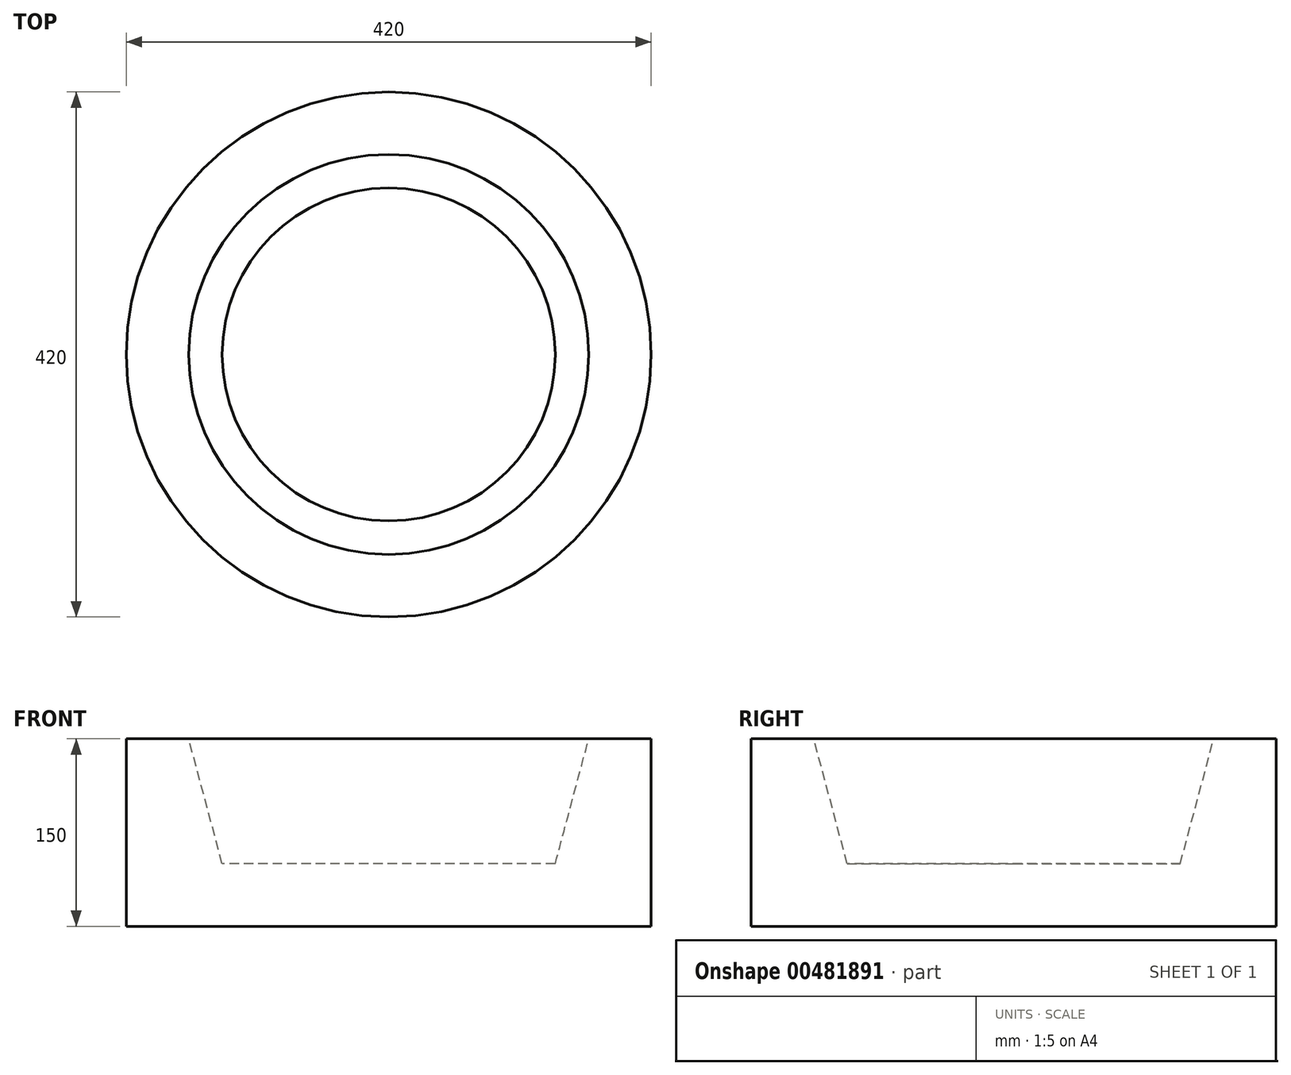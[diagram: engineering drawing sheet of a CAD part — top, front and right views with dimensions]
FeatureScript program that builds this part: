
annotation { "Feature Type Name" : "Feature", "Feature Type Description" : "" }
export const myFeature = defineFeature(function(context is Context, id is Id, definition is map)
    precondition{}
    {
        {
            var Q0;
            Q0=qCreatedBy(makeId("Top.planeOp"),FACE);
            var sketch = newSketch(context, id + "F0", { "sketchPlane" : qUnion([Q0])});
            skCircle(sketch, "E0", {"center": v(0, 0) * mm, "radius": 210 * mm});
            skSolve(sketch);
        }
        {
            var Q0;
            Q0 = qSketchRegion(id + "F0", true);
            extrude(context, id + "F1", {"entities" : qUnion([Q0]), "depth" : 150 * mm});
        }
        {
            var Q0;
            Q0=makeQuery(id+"F1.opExtrude","CAP_FACE",FACE,{"disambiguationData":[OSD([sQuery(id+"F0.wireOp",EDGE,"E0")])],"isStart":false});
            var sketch = newSketch(context, id + "F2", { "sketchPlane" : qUnion([Q0])});
            skCircle(sketch, "E1", {"center": v(0, 0) * mm, "radius": 160 * mm});
            skSolve(sketch);
        }
        {
            var Q0;
            Q0 = qSketchRegion(id + "F2", true);
            extrude(context, id + "F3", {"entities" : qUnion([Q0]), "operationType" : NewBodyOperationType.REMOVE, "oppositeDirection" : true, "depth" : 100 * mm, "hasDraft" : true, "draftAngle" : 15 * degree, "draftPullDirection" : true});
        }
    });
